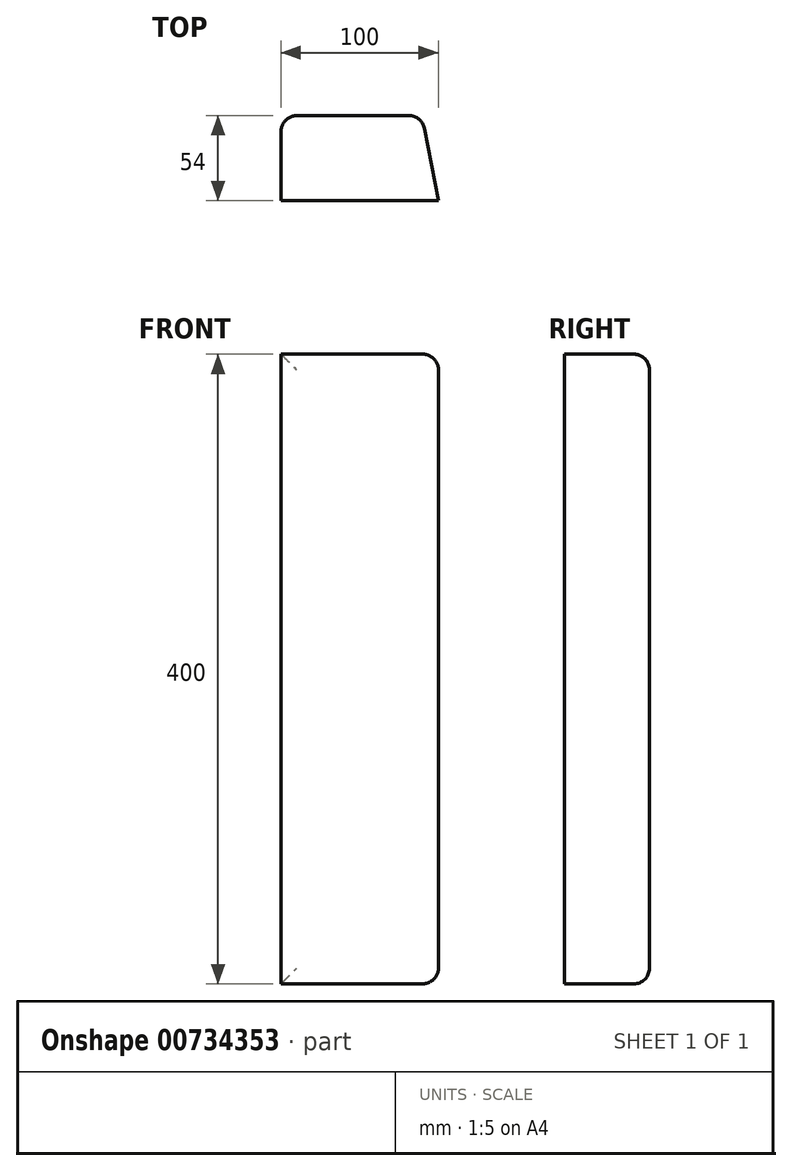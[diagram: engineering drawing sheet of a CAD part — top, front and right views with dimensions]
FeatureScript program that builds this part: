
annotation { "Feature Type Name" : "Feature", "Feature Type Description" : "" }
export const myFeature = defineFeature(function(context is Context, id is Id, definition is map)
    precondition{}
    {
        {
            var Q0;
            Q0=qCreatedBy(makeId("Top.planeOp"),FACE);
            var sketch = newSketch(context, id + "F0", { "sketchPlane" : qUnion([Q0])});
            skLineSegment(sketch, "E0", {"start": v(0, 0) * mm, "end": v(-89.56, 0) * mm});
            skLineSegment(sketch, "E1", {"start": v(-89.56, 0) * mm, "end": v(-89.56, -54) * mm});
            skLineSegment(sketch, "E2", {"start": v(-89.56, -54) * mm, "end": v(10.44, -54) * mm});
            skLineSegment(sketch, "E3", {"start": v(10.44, -54) * mm, "end": v(0, 0) * mm});
            skSolve(sketch);
        }
        {
            var Q0;
            Q0 = qSketchRegion(id + "F0", true);
            extrude(context, id + "F1", {"entities" : qUnion([Q0]), "depth" : 400 * mm, "offsetDistance" : 25 * mm});
        }
        {
            var Q0;
            Q0=makeQuery(id+"F1.opExtrude","SWEPT_EDGE",EDGE,{"disambiguationData":[OSD([sQuery(id+"F0.wireOp",EDGE,"E0"),sQuery(id+"F0.wireOp",EDGE,"E3")])]});
            var Q1;
            Q1=makeQuery(id+"F1.opExtrude","CAP_EDGE",EDGE,{"disambiguationData":[OSD([sQuery(id+"F0.wireOp",EDGE,"E3")])],"isStart":false});
            var Q2;
            Q2=makeQuery(id+"F1.opExtrude","CAP_EDGE",EDGE,{"disambiguationData":[OSD([sQuery(id+"F0.wireOp",EDGE,"E3")])],"isStart":true});
            var Q3;
            Q3=makeQuery(id+"F1.opExtrude","SWEPT_FACE",FACE,{"disambiguationData":[OSD([sQuery(id+"F0.wireOp",EDGE,"E0")])]});
            fillet(context, id + "F2", {"entities" : qUnion([Q0, Q1, Q2, Q3]), "radius" : 10 * mm, "tangentPropagation" : true, "allowEdgeOverflow" : false});
        }
    });
